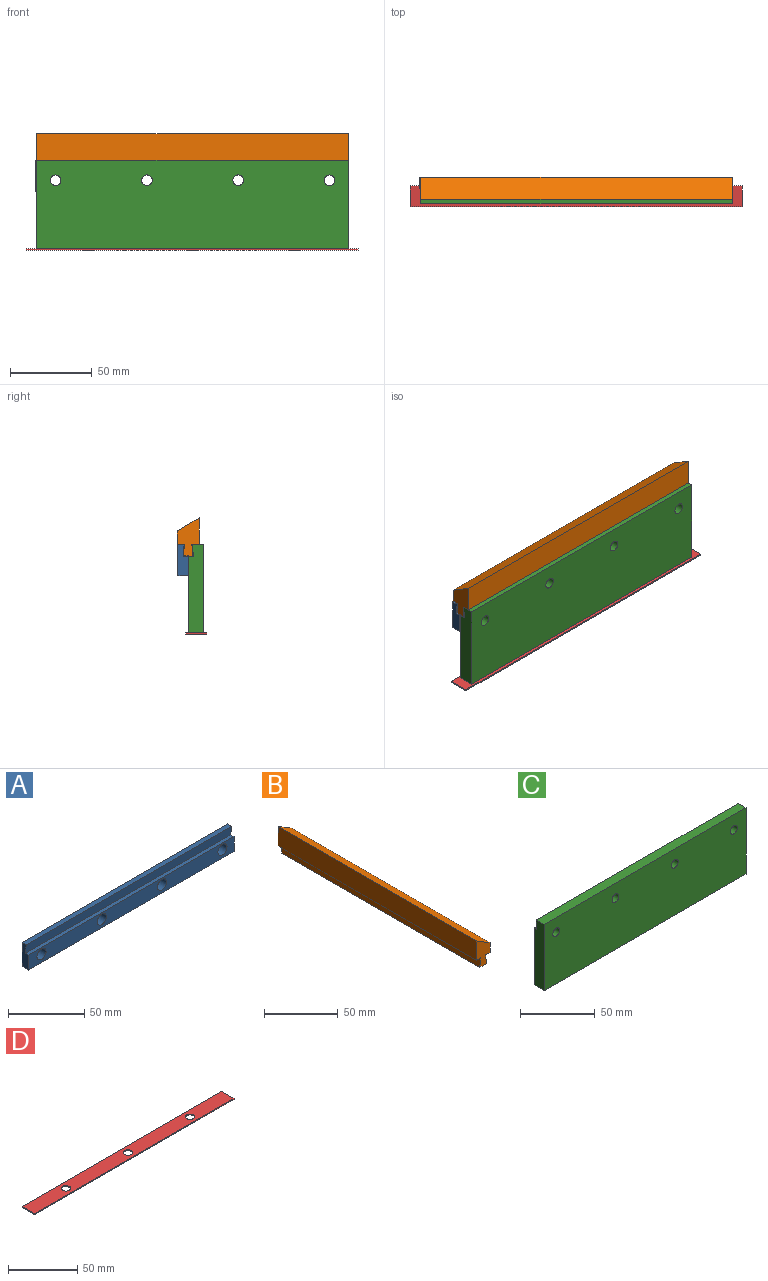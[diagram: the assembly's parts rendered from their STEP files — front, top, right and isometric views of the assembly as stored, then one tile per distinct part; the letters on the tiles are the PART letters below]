
ASSEMBLY  parts=4 mates=3
PART A: 12 faces, bbox 190.5x6.4x19.1 mm
  f0: plane 19.05x6.35mm, normal (1,0,0), area 102mm2, adj f1,f3,f4,f5,f10,f11
  f1: plane 190.5x3.89mm, normal (0,0,1), area 740.3mm2, adj f0,f2,f5,f11
  f2: plane 19.05x6.35mm, normal (-1,0,0), area 102mm2, adj f1,f3,f4,f5,f10,f11
  f3: plane 190.5x6.35mm, normal (0,0,-1), area 1209.7mm2, adj f0,f2,f4,f5
  f4: plane 190.5x12.04mm, normal (0,-1,0), area 2070.1mm2, adj f0,f2,f3,f6,f7,f8,f9,f10
  f5: plane 190.5x19.05mm, normal (0,1,0), area 3405.6mm2, adj f0,f1,f2,f3,f6,f7,f8,f9
  f6: cylinder r=4.22mm len=8.43mm, axis (0,-1,0), area 168.2mm2, adj f4,f5
  f7: cylinder r=4.22mm len=8.43mm, axis (0,-1,0), area 168.2mm2, adj f4,f5
  f8: cylinder r=4.22mm len=8.43mm, axis (0,-1,0), area 168.2mm2, adj f4,f5
  f9: cylinder r=4.22mm len=8.43mm, axis (0,-1,0), area 168.2mm2, adj f4,f5
  f10: plane 190.5x2.95mm, normal (0,0,1), area 561.3mm2, adj f0,f2,f4,f11
  f11: plane 190.5x7.01mm, normal (0,-1,-0.07), area 1338.6mm2, adj f0,f1,f2,f10
PART B: 10 faces, bbox 13.3x190.5x23.8 mm
  f0: plane 190.5x4.13mm, normal (0,0,-1), area 786.3mm2, adj f1,f7,f8,f9
  f1: plane 190.5x7.62mm, normal (-1,0,0.08), area 1456.1mm2, adj f0,f2,f8,f9
  f2: plane 190.5x6.22mm, normal (0,0,-1), area 1185.5mm2, adj f1,f3,f8,f9
  f3: plane 190.5x7.62mm, normal (1,0,0.07), area 1455.3mm2, adj f2,f4,f8,f9
  f4: plane 190.5x4.08mm, normal (0,0,-1), area 776.6mm2, adj f3,f5,f8,f9
  f5: plane 190.5x8.13mm, normal (1,0,0), area 1548.4mm2, adj f4,f6,f8,f9
  f6: plane 190.5x13.28mm, normal (0.52,0,0.86), area 2956.7mm2, adj f5,f7,f8,f9
  f7: plane 190.5x16.15mm, normal (-1,0,0), area 3077.4mm2, adj f0,f6,f8,f9
  f8: plane 23.77x13.28mm, normal (0,-1,0), area 204.4mm2, adj f0,f1,f2,f3,f4,f5,f6,f7
  f9: plane 23.77x13.28mm, normal (0,1,0), area 204.4mm2, adj f0,f1,f2,f3,f4,f5,f6,f7
PART C: 18 faces, bbox 190.5x9.5x54.1 mm
  f0: plane 54.11x9.53mm, normal (1,0,0), area 497.1mm2, adj f2,f3,f4,f5,f10,f11
  f1: plane 54.11x9.53mm, normal (-1,0,0), area 497.1mm2, adj f2,f3,f4,f5,f10,f11
  f2: plane 190.5x9.53mm, normal (0,0,-1), area 1707mm2, adj f0,f1,f4,f5,f13,f15,f17
  f3: plane 190.5x7.32mm, normal (0,0,1), area 1393.5mm2, adj f0,f1,f4,f10
  f4: plane 190.5x54.11mm, normal (0,-1,0), area 10175mm2, adj f0,f1,f2,f3,f6,f7,f8,f9
  f5: plane 190.5x46.63mm, normal (0,1,0), area 8750mm2, adj f0,f1,f2,f6,f7,f8,f9,f11
  f6: cylinder r=3.26mm len=9.53mm, axis (0,-1,0), area 195.3mm2, adj f4,f5
  f7: cylinder r=3.26mm len=9.53mm, axis (0,-1,0), area 195.3mm2, adj f4,f5
  f8: cylinder r=3.26mm len=9.53mm, axis (0,-1,0), area 195.3mm2, adj f4,f5
  f9: cylinder r=3.26mm len=9.53mm, axis (0,-1,0), area 195.3mm2, adj f4,f5
  f10: plane 190.5x7.48mm, normal (0,1,-0.06), area 1428mm2, adj f0,f1,f3,f11
  f11: plane 190.5x2.69mm, normal (0,0,1), area 512.9mm2, adj f0,f1,f5,f10
  f12: cone r=0mm half-angle=59deg, axis (0,0,-1), area 41.8mm2, adj f13
  f13: cylinder r=3.38mm len=12.7mm, axis (0,0,-1), area 269.6mm2, adj f2,f12
  f14: cone r=0mm half-angle=59deg, axis (0,0,-1), area 41.8mm2, adj f15
  f15: cylinder r=3.38mm len=12.7mm, axis (0,0,-1), area 269.6mm2, adj f2,f14
  f16: cone r=0mm half-angle=59deg, axis (0,0,-1), area 41.8mm2, adj f17
  f17: cylinder r=3.38mm len=12.7mm, axis (0,0,-1), area 269.6mm2, adj f2,f16
PART D: 9 faces, bbox 203.2x12.7x0.8 mm
  f0: plane 203.2x12.7mm, normal (0,0,1), area 2473.1mm2, adj f1,f3,f4,f5,f6,f7,f8
  f1: plane 12.7x0.79mm, normal (-1,0,0), area 10.1mm2, adj f0,f2,f4,f5
  f2: plane 203.2x12.7mm, normal (0,0,-1), area 2473.1mm2, adj f1,f3,f4,f5,f6,f7,f8
  f3: plane 12.7x0.79mm, normal (1,0,0), area 10.1mm2, adj f0,f2,f4,f5
  f4: plane 203.2x0.79mm, normal (0,-1,0), area 161.3mm2, adj f0,f1,f2,f3
  f5: plane 203.2x0.79mm, normal (0,1,0), area 161.3mm2, adj f0,f1,f2,f3
  f6: cylinder r=3.38mm len=6.76mm, axis (0,0,1), area 16.8mm2, adj f0,f2
  f7: cylinder r=3.38mm len=6.76mm, axis (0,0,1), area 16.8mm2, adj f0,f2
  f8: cylinder r=3.38mm len=6.76mm, axis (0,0,1), area 16.8mm2, adj f0,f2
PLACE A t=(-28.57,56.45,11.46)mm
PLACE B rot(axis=(0,0,1),90deg) t=(-27.86,43.46,30.66)mm
PLACE C t=(-27.86,50.1,-23.6)mm
PLACE D t=(-34.53,51.65,-24.39)mm
MATE fastened A.f9 <-> C.f9  axis (0,-1,0) through (151.23,50.1,18.38)mm
MATE fastened D.f6 <-> C.f14  axis (0,0,1) through (67.07,45.3,-23.6)mm
MATE fastened B.f2 <-> C.f11  axis (0,0,-1) through (67.39,50.1,23.04)mm
